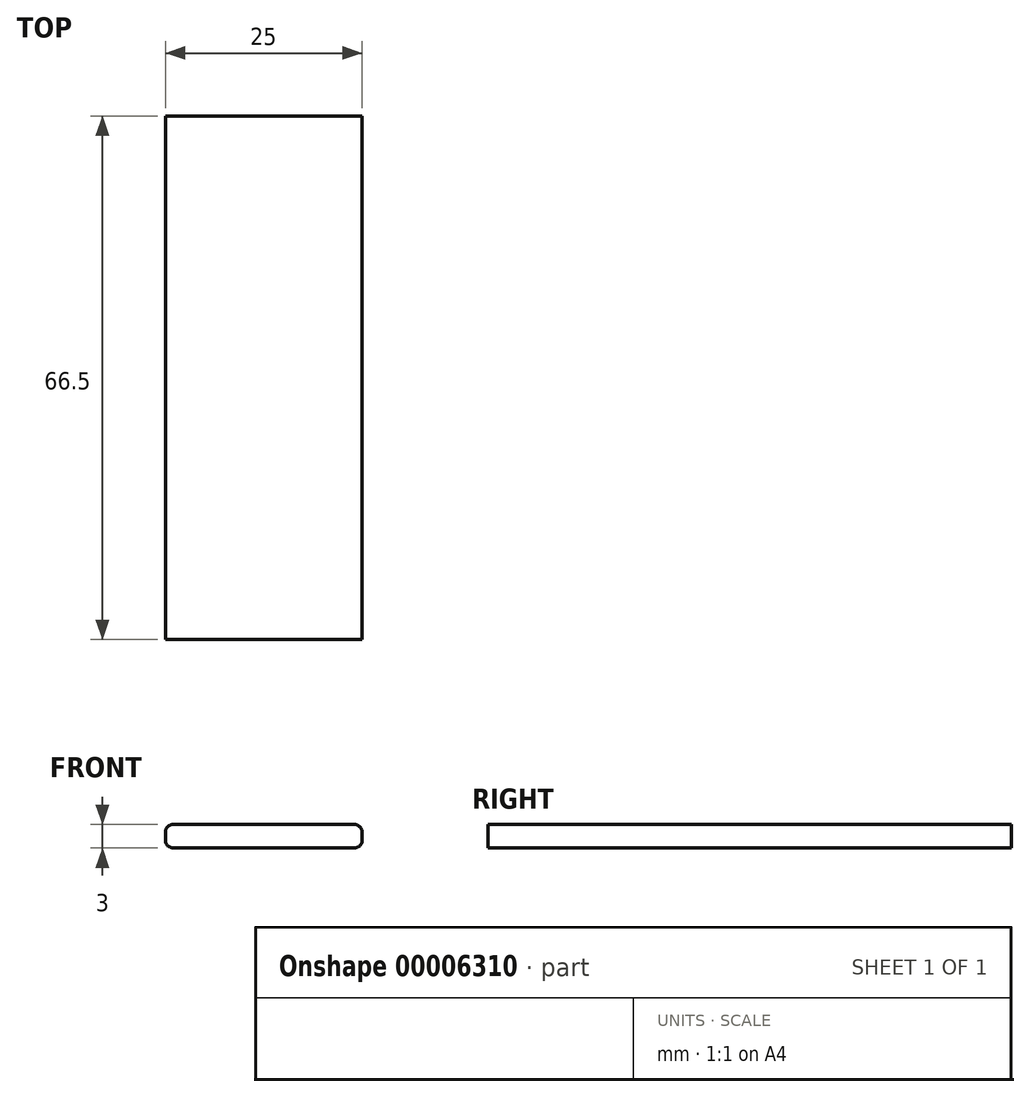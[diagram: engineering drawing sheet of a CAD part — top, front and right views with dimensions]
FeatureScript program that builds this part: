
annotation { "Feature Type Name" : "Feature", "Feature Type Description" : "" }
export const myFeature = defineFeature(function(context is Context, id is Id, definition is map)
    precondition{}
    {
        {
            var Q0;
            Q0=qCreatedBy(makeId("Front.planeOp"),FACE);
            var sketch = newSketch(context, id + "F0", { "sketchPlane" : qUnion([Q0])});
            skLineSegment(sketch, "E0.bottom", {"start": v(1, 0) * mm, "end": v(24, 0) * mm});
            skLineSegment(sketch, "E0.top", {"start": v(1, 3) * mm, "end": v(24, 3) * mm});
            skLineSegment(sketch, "E0.left", {"start": v(0, 1) * mm, "end": v(0, 2) * mm});
            skLineSegment(sketch, "E0.right", {"start": v(25, 1) * mm, "end": v(25, 2) * mm});
            skPoint(sketch, "E1.visualSharp", {"position": v(0, 3) * mm});
            skArc(sketch, "E1.filletArc", {"start": v(1, 3) * mm, "mid": v(0.3, 2.7) * mm, "end": v(0, 2) * mm});
            skPoint(sketch, "E2.visualSharp", {"position": v(0, 0) * mm});
            skArc(sketch, "E2.filletArc", {"start": v(0, 1) * mm, "mid": v(0.3, 0.3) * mm, "end": v(1, 0) * mm});
            skPoint(sketch, "E3.visualSharp", {"position": v(25, 3) * mm});
            skArc(sketch, "E3.filletArc", {"start": v(25, 2) * mm, "mid": v(24.7, 2.7) * mm, "end": v(24, 3) * mm});
            skPoint(sketch, "E4.visualSharp", {"position": v(25, 0) * mm});
            skArc(sketch, "E4.filletArc", {"start": v(24, 0) * mm, "mid": v(24.7, 0.3) * mm, "end": v(25, 1) * mm});
            skSolve(sketch);
        }
        {
            var Q0;
            Q0=makeQuery(id+"F0.imprint","IMPRINT",FACE,{"disambiguationData":[TD([[makeQuery(id+"F0.imprint","IMPRINT",EDGE,{"derivedFrom":sQuery(id+"F0.wireOp",EDGE,"E0.bottom")}),1.0]])]});
            extrude(context, id + "F1", {"entities" : qUnion([Q0]), "endBound" : BoundingType.SYMMETRIC, "depth" : (15.5 * 3 + 20) * mm});
        }
        {
            var Q0;
            Q0=makeQuery(id+"F1.opExtrude","SWEPT_BODY",BODY,{"disambiguationData":[OSD([sQuery(id+"F0.wireOp",EDGE,"E0.bottom"),sQuery(id+"F0.wireOp",EDGE,"E0.top"),sQuery(id+"F0.wireOp",EDGE,"E0.left"),sQuery(id+"F0.wireOp",EDGE,"E0.right"),sQuery(id+"F0.wireOp",EDGE,"E1.filletArc"),sQuery(id+"F0.wireOp",EDGE,"E2.filletArc"),sQuery(id+"F0.wireOp",EDGE,"E3.filletArc"),sQuery(id+"F0.wireOp",EDGE,"E4.filletArc")])]});
            transform(context, id + "F2", {"entities" : qUnion([Q0]), "transformType" : TransformType.TRANSLATION_3D, "dx" : 0 * mm, "dy" : 0 * mm, "dz" : 0 * mm, "makeCopy" : true});
        }
        {
            var Q0;
            Q0=makeQuery(id+"F2.opPattern","COPY",BODY,{"derivedFrom":makeQuery(id+"F1.opExtrude","SWEPT_BODY",BODY,{"disambiguationData":[OSD([sQuery(id+"F0.wireOp",EDGE,"E0.bottom"),sQuery(id+"F0.wireOp",EDGE,"E0.top"),sQuery(id+"F0.wireOp",EDGE,"E0.left"),sQuery(id+"F0.wireOp",EDGE,"E0.right"),sQuery(id+"F0.wireOp",EDGE,"E1.filletArc"),sQuery(id+"F0.wireOp",EDGE,"E2.filletArc"),sQuery(id+"F0.wireOp",EDGE,"E3.filletArc"),sQuery(id+"F0.wireOp",EDGE,"E4.filletArc")])]}),"instanceName":"1"});
            deleteBodies(context, id + "F3", {"entities" : qUnion([Q0])});
        }
    });
